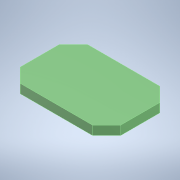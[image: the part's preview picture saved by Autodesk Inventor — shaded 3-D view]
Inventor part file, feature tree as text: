
AUTODESK INVENTOR PART (.ipt)
format: ipt  version: 2021 (Build 250183000, 183)  size: 105,984 bytes
history: native  units: mm
features: extrude x1, sketch x1
ambient origin geometry x8: Origin, YZ Plane, XZ Plane, XY Plane, X Axis, Y Axis, Z Axis, Center Point
bodies: Solid1 (feature_tree)
feature tree (2):
  extrude  "Extrusion1"  Depth=14.2mm
  sketch  "Sketch1"  dims[d0=21.2mm d1=14.2mm d2=3.0mm d3=3.0mm d10=1.9mm d11=0.0mm d12=20.788939mm]
